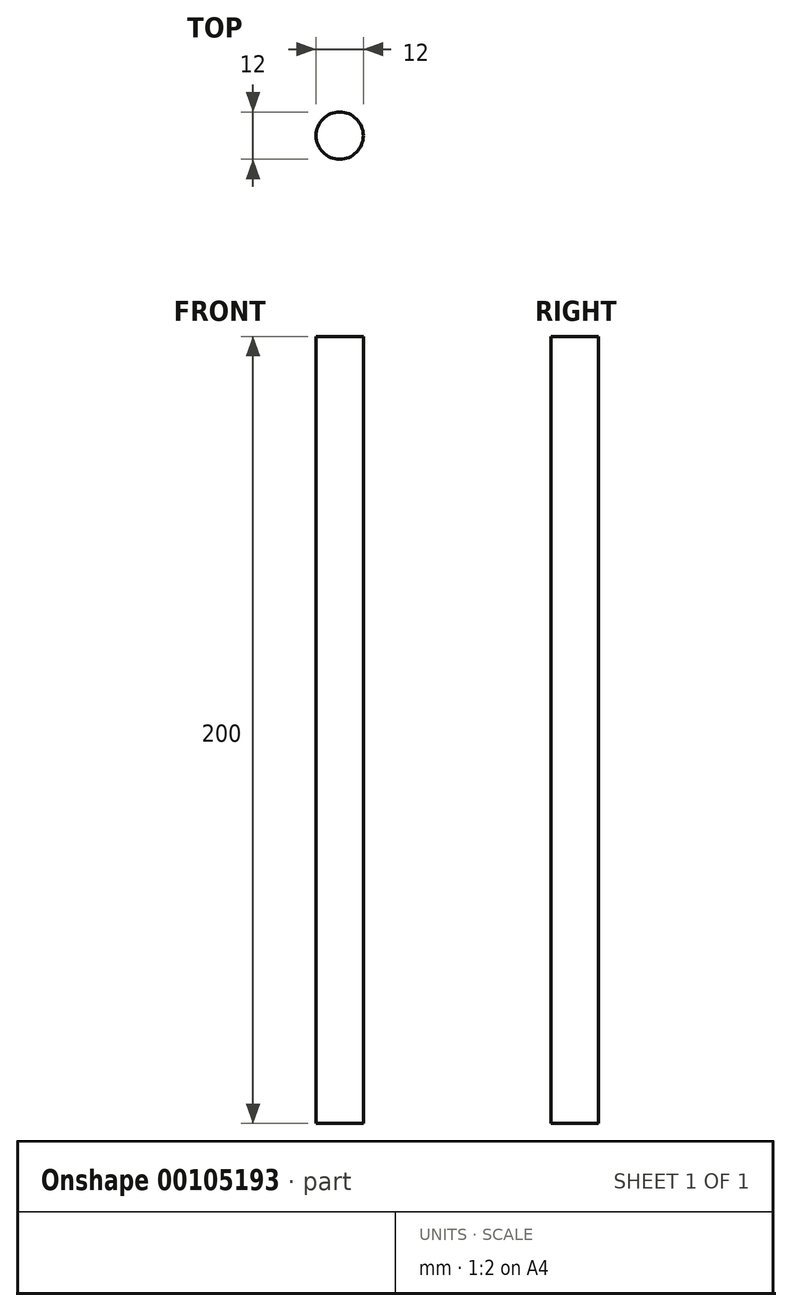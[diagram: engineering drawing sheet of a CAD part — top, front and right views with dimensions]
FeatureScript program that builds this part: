
annotation { "Feature Type Name" : "Feature", "Feature Type Description" : "" }
export const myFeature = defineFeature(function(context is Context, id is Id, definition is map)
    precondition{}
    {
        {
            var Q0;
            Q0=qCreatedBy(makeId("Top.planeOp"),FACE);
            var sketch = newSketch(context, id + "F0", { "sketchPlane" : qUnion([Q0])});
            skCircle(sketch, "E0", {"center": v(0, 0) * mm, "radius": 6 * mm});
            skSolve(sketch);
        }
        {
            var Q0;
            Q0=qSketchRegion(id+"F0",true);
            extrude(context, id + "F1", {"entities" : qUnion([Q0]), "depth" : 190 * mm});
        }
        {
            var Q0;
            Q0=makeQuery(id+"F1.opExtrude","CAP_FACE",FACE,{"disambiguationData":[OSD([sQuery(id+"F0.wireOp",EDGE,"E0")])],"isStart":false});
            var sketch = newSketch(context, id + "F2", { "sketchPlane" : qUnion([Q0])});
            skSolve(sketch);
        }
        {
            var Q0;
            Q0=makeQuery(id+"F2.imprint","IMPRINT",FACE,{"disambiguationData":[TD([[makeQuery(id+"F2.imprint","IMPRINT",EDGE,{"derivedFrom":makeQuery(id+"F1.opExtrude","CAP_EDGE",EDGE,{"disambiguationData":[OSD([sQuery(id+"F0.wireOp",EDGE,"E0")])],"isStart":false})}),1.0]])]});
            var sketch = newSketch(context, id + "F3", { "sketchPlane" : qUnion([Q0])});
            skCircle(sketch, "E1", {"center": v(0, 0) * mm, "radius": 6 * mm});
            skSolve(sketch);
        }
        {
            var Q0;
            Q0=qSketchRegion(id+"F3",true);
            extrude(context, id + "F4", {"entities" : qUnion([Q0]), "operationType" : NewBodyOperationType.ADD, "depth" : 5 * mm});
        }
        {
            var Q0;
            Q0=qSketchRegion(id+"F3",true);
            extrude(context, id + "F5", {"entities" : qUnion([Q0]), "operationType" : NewBodyOperationType.ADD, "oppositeDirection" : true, "depth" : 195 * mm});
        }
        {
            var Q0;
            Q0=makeQuery(id+"F1.opExtrude","SWEPT_BODY",BODY,{"disambiguationData":[OSD([sQuery(id+"F0.wireOp",EDGE,"E0")])]});
            transform(context, id + "F6", {"entities" : qUnion([Q0]), "transformType" : TransformType.TRANSLATION_3D, "dx" : 0 * mm, "dy" : 0 * mm, "dz" : 0 * mm, "makeCopy" : true});
        }
    });
